# Revit family: LAMP_HANCE DOWNLIGHT SEMIRECESSED FLOOD 1000_2000 (DALI)
name_source: partatom
category: Modelos genéricos
revit_build: Autodesk Revit 2015 (Build: 20140606_1530(x64)
units: mm (PartAtom-declared; Revit-internal decimal feet)

## types (8) — shared parameters
CRI = 80
Comentarios de tipo = Availability of tilting between 0º and 85º when placed in a project.
Diameter = 143 mm
Elevación por defecto = 1219 mm
Fabricante = LAMP
Gear = Adjustable DALI
Installation instructions = https://www.lamp.es
Insulation class = II
LED Lifetime = 50.000 L80 B10
Lamp = COB LED
Last update = 22/11/2019
Luminaire type = Indoor - Recessed downlight
MacAdam = 3
Manufacturer URL = http://www.lamp.es
Manufacturer country = Spain
Manufacturer name = LAMP
Material interior aro = LAMP_Aluminio Hance Negro
Model explanation = Availability of tilting between 0º and 85º when placed in a project.
Power Supply = 220-240V 50/60Hz
Product URL = https://www.lamp.es
Product datasheet = http://www.lamp.es
Protection rating = IP20
Recessed diameter = 132 mm  [stored 0.433071 ft]
Type = COB PHILIPS
Weight = 0.79 kg

## per-type parameters (varying)
| type | Descripción | Efficacy | Finish | IEE | Initial color | Initial intensity | Material aro | Modelo | Photometric web file | Plum | Power | Product code |
| 675LM 4000K 1000 BLACK | HANCE DOWN SEMIREC 1000 NW FL DALI BK. | 89 lm/W | Texturised white RAL 9010 | A+ | 4000 K | 675 lm | LAMP_Aluminio Hance Negro | HD1SR10FL840DBB | Cuerpo Hance BASE (tilting)_FL : 675LM 4000K 1000 BLACK | 8 W | 7 W | HD1SR10FL840DBB |
| 675LM 4000K 1000 WHITE | HANCE DOWN SEMIREC 1000 NW FL DALI WH. | 89 lm/W | Texturised black RAL 9011 | A+ | 4000 K | 675 lm | LAMP_Aluminio Hance Blanco | HD1SR10FL840DBW | Cuerpo Hance BASE (tilting)_FL : 675LM 4000K 1000 WHITE | 8 W | 7 W | HD1SR10FL840DBW |
| 697LM 3000K 1000 BLACK | HANCE DOWN SEMIREC 1000 WW FL DALI BK. | 90 lm/W | Texturised white RAL 9010 | A+ | 3000 K | 697 lm | LAMP_Aluminio Hance Negro | HD1SR10FL830DBB | Cuerpo Hance BASE (tilting)_FL : 697LM 3000K 1000 BLACK | 8 W | 7 W | HD1SR10FL830DBB |
| 697LM 3000K 1000 WHITE | HANCE DOWN SEMIREC 1000 WW FL DALI WH. | 90 lm/W | Texturised black RAL 9011 | A+ | 3000 K | 697 lm | LAMP_Aluminio Hance Blanco | HD1SR10FL830DBW | Cuerpo Hance BASE (tilting)_FL : 697LM 3000K 1000 WHITE | 8 W | 7 W | HD1SR10FL830DBW |
| 1445LM 3000K 2000 BLACK | HANCE DOWN SEMIREC 2000 WW FL DALI BK. | 70 lm/W | Texturised black RAL 9011 | A | 3000 K | 1445 lm | LAMP_Aluminio Hance Negro | HD1SR20FL830DBB | Cuerpo Hance BASE (tilting)_FL : 1445LM 3000K 2000 BLACK | 21 W | 18 W | HD1SR20FL830DBB |
| 1445LM 3000K 2000 WHITE | HANCE DOWN SEMIREC 2000 WW FL DALI WH. | 70 lm/W | Texturised white RAL 9010 | A | 3000 K | 1445 lm | LAMP_Aluminio Hance Blanco | HD1SR20FL830DBW | Cuerpo Hance BASE (tilting)_FL : 1445LM 3000K 2000 WHITE | 21 W | 18 W | HD1SR20FL830DBW |
| 1466LM 4000K 2000 BLACK | HANCE DOWN SEMIREC 2000 NW FL DALI BK. | 71 lm/W | Texturised black RAL 9011 | A | 4000 K | 1466 lm | LAMP_Aluminio Hance Negro | HD1SR20FL840DBB | Cuerpo Hance BASE (tilting)_FL : 1466LM 4000K 2000 BLACK | 21 W | 18 W | HD1SR20FL840DBB |
| 1466LM 4000K 2000 WHITE | HANCE DOWN SEMIREC 2000 NW FL DALI WH. | 71 lm/W | Texturised white RAL 9010 | A | 4000 K | 1466 lm | LAMP_Aluminio Hance Blanco | HD1SR20FL840DBW | Cuerpo Hance BASE (tilting)_FL : 1466LM 4000K 2000 WHITE | 21 W | 18 W | HD1SR20FL840DBW |

note: [stored X ft] marks values corroborated as IEEE doubles in the binary element streams (Revit-internal decimal feet)
